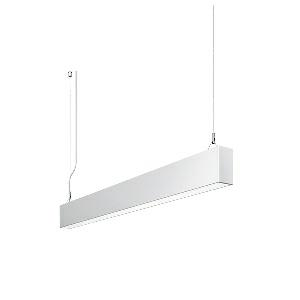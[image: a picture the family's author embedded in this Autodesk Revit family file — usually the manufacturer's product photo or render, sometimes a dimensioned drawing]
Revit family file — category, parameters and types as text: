
# Revit family: idoo_line_-_ilp_3000_vtl_d_00806448_acb8
name_source: partatom
category: Lighting Fixtures
units: mm (PartAtom-declared; Revit-internal decimal feet)

## family parameters
Cut with Voids When Loaded = No
Host = Face
Light Source = No
Part Type = Normal
Room Calculation Point = No
Round Connector Dimension = Use Diameter
Shared = No

## types (1)
- IDOO.line - ILP 3000/VTL/D (1 x LED, 3150 lm, 2700-6500K)
    Apparent Load = 32 VA
    Approval mark = CE
    CIE Flux Codes = 66 91 98 40 100
    Color Rendering = 90-100
    Color Temperature = 2700-6500K
    Control Gear = Electronic ballast
    Default Elevation = 1800 mm
    Description = ILP 3000/VTL/D|Suspended luminaire|light source: LED|connected load: 220-240 V, 50/60 Hz|Power consumption: approx. 32 W|standby: approx. 0,25|luminous flux: 3150 lm|luminous efficacy: 98 lm/W|light distribution: Direct/indirect|direct ratio: approx. 40 %|colour temperature: Cold white, ca. 2700-6500 K|color rendering index (CRI): >= 90|chromaticity tolerance:  3 SDCM|System of protection: IP 40|technology: Continuously dimmable|luminaire body|material: Sectional aluminium|colour: White|lamp cover: Acrylic (PMMA), Clear|mains lead: 2.00 m With free stranded wires|Fastening: Steel cable 0.3 - 0.7 m|glare control: Prism aperture|luminance(L65): <= 2700 cd/m|unified glare rating(4H 8H): <=  16|special features: Specified values at approx. 4000 K, DALI Load 1x, External control required for Dali Device type 8, Flicker-free, Constant luminous flux between 2700 and 6500 K, Constant colour temperature over the whole dimming range, Suitable as emergency lighting|
    Frequency = 50 Hz
    Height = 110 mm
    Lamp = 1 x LED
    Lamp Light Flux = 3150 lm
    Lamp count = 1
    Length = 1134 mm
    Luminous efficacy = 98 lm/W
    Manufacturer = Waldmann
    ModVariant = No
    Model = 00806448
    Mounting Place = Ceiling
    Mounting Type = Pendant
    Number of Poles = 1
    OnlyDefault = Yes
    Power Factor = 1
    Product Name = IDOO.line - ILP 3000/VTL/D
    Product group = Suspended luminaire
    ProductGroupID = 9
    Protection Class = Protection class I
    Protection Degree = IP 40
    RLX_Detail_Level = 1
    RLX_Emergency_Light_Flux = 0 lm
    RLX_Emergency_Type = 0
    RLX_Emergency_Type_DB = No
    RlxData = <blob elided: 19333 chars, md5=d97e21f1>
    Socket = socket
    Standby Power = 0 W
    System Light Flux = 3150 lm
    System Power = 32 W
    Type Comments = Product without accessories
    Type Image = 113289000-00692516.jpg
    URL = http://relux.com
    VarID = ---
    Voltage = 230 V
    Voltage Range = 220-240 V
    Weight = 0.00 kg
    Width = 60 mm  [stored 0.19685 ft]

note: [stored X ft] marks values corroborated as IEEE doubles in the binary element streams (Revit-internal decimal feet)

## geometry (parser evidence)
native form markers: Blend x4, Sweep x12
no freeform markers — native parametric forms only
